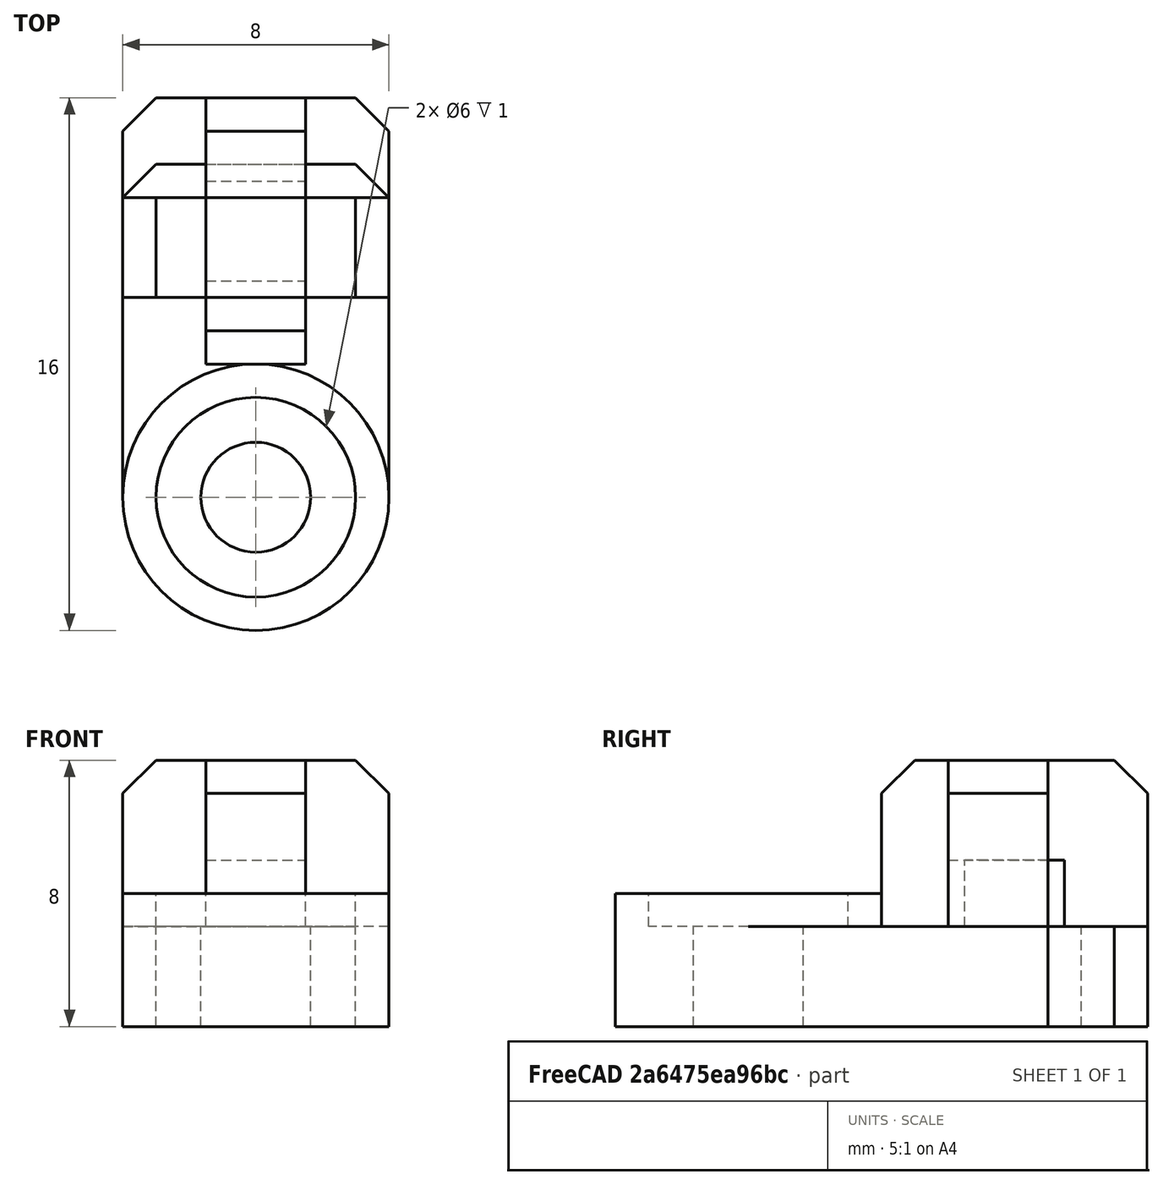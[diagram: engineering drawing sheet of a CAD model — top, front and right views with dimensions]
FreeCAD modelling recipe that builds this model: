
FCSTD DOCUMENT  (FreeCAD 0.18R16146 (Git))
Label: cable-mounter
License: All rights reserved
LicenseURL: http://en.wikipedia.org/wiki/All_rights_reserved
objects: Part::Cylinder×6, Part::Cut×5, Part::Box×4, Part::Chamfer×3, Part::MultiFuse×2, Part::Feature×1
note: 21 computed .brp shape members not serialized (recipe doc carries the construction recipe); baked Part::Feature solids carry a one-line shape summary decoded from their .brp

FEATURE [Part::Cylinder] Cylinder
  Angle = 360
  AttacherType = Attacher::AttachEngine3D
  Height = 10
  Radius = 1.65
FEATURE [Part::Cylinder] Cylinder001
  Angle = 360
  AttacherType = Attacher::AttachEngine3D
  Height = 4
  Radius = 4
FEATURE [Part::Box] Box  label="Cube"
  AttacherType = Attacher::AttachEngine3D
  Height = 3
  Length = 8
  Placement = pos=(-4,0,0) rot=(0,0,1;0rad)
  Width = 10
FEATURE [Part::Box] Box001  label="Cube001"
  AttacherType = Attacher::AttachEngine3D
  Height = 8
  Length = 8
  Placement = pos=(-4,6,0) rot=(0,0,1;0rad)
  Width = 3
FEATURE [Part::Box] Box002  label="Cube002"
  AttacherType = Attacher::AttachEngine3D
  Height = 5
  Length = 3
  Placement = pos=(-1.5,6,0) rot=(0,0,1;0rad)
  Width = 3
FEATURE [Part::Cut] Cut
  Base = -> Box001
  Tool = -> Box002
FEATURE [Part::Chamfer] Chamfer
  Base = -> Cut
  Edges = 2 edges r=1: [Edge2,Edge13]
FEATURE [Part::Cylinder] Cylinder002
  Angle = 360
  AttacherType = Attacher::AttachEngine3D
  Height = 4
  Radius = 4
FEATURE [Part::Cylinder] Cylinder003
  Angle = 360
  AttacherType = Attacher::AttachEngine3D
  Height = 10
  Radius = 1.65
FEATURE [Part::Cylinder] Cylinder004
  Angle = 360
  AttacherType = Attacher::AttachEngine3D
  Height = 1
  Placement = pos=(0,0,3) rot=(0,0,1;0rad)
  Radius = 3
FEATURE [Part::Cut] Cut001
  Base = -> Cylinder001
  Tool = -> Cylinder004
FEATURE [Part::Feature] Chamfer002
  Placement = pos=(-8.5,8,0) rot=(0,0,1;4.71239rad)
  shape: bbox 3 x 8 x 8 mm, 12 faces (baked)
FEATURE [Part::Cylinder] Cylinder005
  Angle = 360
  AttacherType = Attacher::AttachEngine3D
  Height = 1
  Placement = pos=(0,0,3) rot=(0,0,1;0rad)
  Radius = 3
FEATURE [Part::Cut] Cut003
  Base = -> Cylinder002
  Tool = -> Cylinder005
FEATURE [Part::Box] Box003  label="Cube003"
  AttacherType = Attacher::AttachEngine3D
  Height = 3
  Length = 8
  Placement = pos=(-4,0,0) rot=(0,0,1;0rad)
  Width = 12
FEATURE [Part::Chamfer] Chamfer003
  Base = -> Box003
  Edges = 2 edges r=1: [Edge3,Edge7]
FEATURE [Part::MultiFuse] Fusion001
  Shapes = -> [Cut003,Chamfer003,Chamfer002]
FEATURE [Part::Cut] Cut004  label="type-2"
  Base = -> Fusion001
  Tool = -> Cylinder003
FEATURE [Part::Chamfer] Chamfer004
  Base = -> Box
  Edges = 2 edges r=1: [Edge3,Edge7]
FEATURE [Part::MultiFuse] Fusion
  Shapes = -> [Chamfer004,Chamfer,Cut001]
FEATURE [Part::Cut] Cut005  label="type-1"
  Base = -> Fusion
  Tool = -> Cylinder
